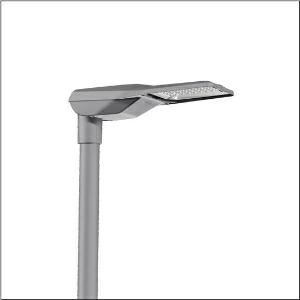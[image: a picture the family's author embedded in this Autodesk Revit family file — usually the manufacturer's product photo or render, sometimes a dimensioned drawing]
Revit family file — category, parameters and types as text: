
# Revit family: streetlight_sl_21_iq_mini___p1_0a_5xe2a31g08gb_9f18
name_source: partatom
category: Lighting Fixtures
units: mm (PartAtom-declared; Revit-internal decimal feet)

## family parameters
Cut with Voids When Loaded = No
Host = Face
Light Source = No
Part Type = Normal
Room Calculation Point = No
Round Connector Dimension = Use Diameter
Shared = No

## types (1)
- --- (1 x LED, 5680 lm, 37.1 W, 3000K)
    Apparent Load = 37 VA
    CIE Flux Codes = 21 50 90 100 100
    Color Rendering = 70
    Color Temperature = 3000K
    Default Elevation = 1800 mm
    Description = Streetlight SL 21 iQ mini, mast luminaire, primary light control with lens, of PMMA, primary optical cover: cover, of toughened safety glass, transparent, light distribution: P1.0a, light emission: direct distribution, primary light characteristic: asymmetric, installation type: post-top, side-entry, LED, High Power LED, rated luminous flux: 5.680lm, luminous efficacy: 153lm/W, light colour: 730, colour temperature: 3000K, control: Street-Remote, Auto-Match, Temp-Guard, Lumen-Switch, Night-Set, Smart-Wire, Light-Fading, Desk-Remote (wireless, voltage-free reading and setting of iQ features in the workshop via application-optimized NFC function/RFID function), optimised constant luminous flux control (CLO 2.0), presetting dimming linear, mains connection: 220..240V, AC, 50/60Hz, start of lifetime: 37W, end of service life: 39W, reduction: 18W, luminaire housing, of diecast aluminium, powder-coated, Siteco® metallic grey (DB 702S), corrosivity category C5 mid according to DIN EN ISO 12944, please order mast flange separately, inclination adjustable: 0°, 5°, 10°, 15°, sealing non-destructively replaceable, multi-level sealing system, length: 628mm, width: 235mm, height: 110mm, mast flange for spigot size: 42mm (side-entry): 5XC10008XM4, 60/48mm (side-entry/post-top): 5XC10108XM2, 76/60mm (side-entry/post-top): 5XC10108XM1, protection rating (complete): IP66, insulation class (complete): insulation class II (safety insulation), certification: CE, ENEC, ENEC+, VDE, impact resistance: IK09, permissible operating ambient temperature for outdoor applications: -40..+50°C, standard-compliant lighting for roads and squares, packaging unit: 1 piece

Light Distribution: P1.0a
    Height = 110 mm
    Lamp = 1 x LED
    Lamp Light Flux = 5680 lm
    Lamp Power = 37.1 W
    Lamp count = 1
    Length = 625 mm
    Luminous efficacy = 153 lm/W
    Manufacturer = Siteco
    ModVariant = No
    Model = 5XE2A31G08GB
    Number of Poles = 1
    OnlyDefault = Yes
    Power Factor = 1
    Product Name = Streetlight SL 21 iQ mini | P1.0a
    Product group = mast luminaire | pylon top
    ProductGroupID = 6100
    Protection Class = Protection class II
    Protection Degree = IP 66
    RLX_Detail_Level = 1
    RLX_Emergency_Light_Flux = 0 lm
    RLX_Emergency_Type = 0
    RLX_Emergency_Type_DB = No
    RlxData = <blob elided: 103657 chars, md5=15aa289e>
    Socket = socket
    Standby Power = 0 W
    System Light Flux = 5680 lm
    System Power = 37 W
    Type Comments = factory setting: luminous flux: 100 % | dim-lin: 254 | 385 mA
    Type Image = l_1003519.jpg
    URL = http://relux.com
    VarID = @adj_138645
    Voltage = 0 V
    Weight = 0.00 kg
    Width = 234 mm

## geometry (parser evidence)
native form markers: Blend x4, Sweep x9
no freeform markers — native parametric forms only
